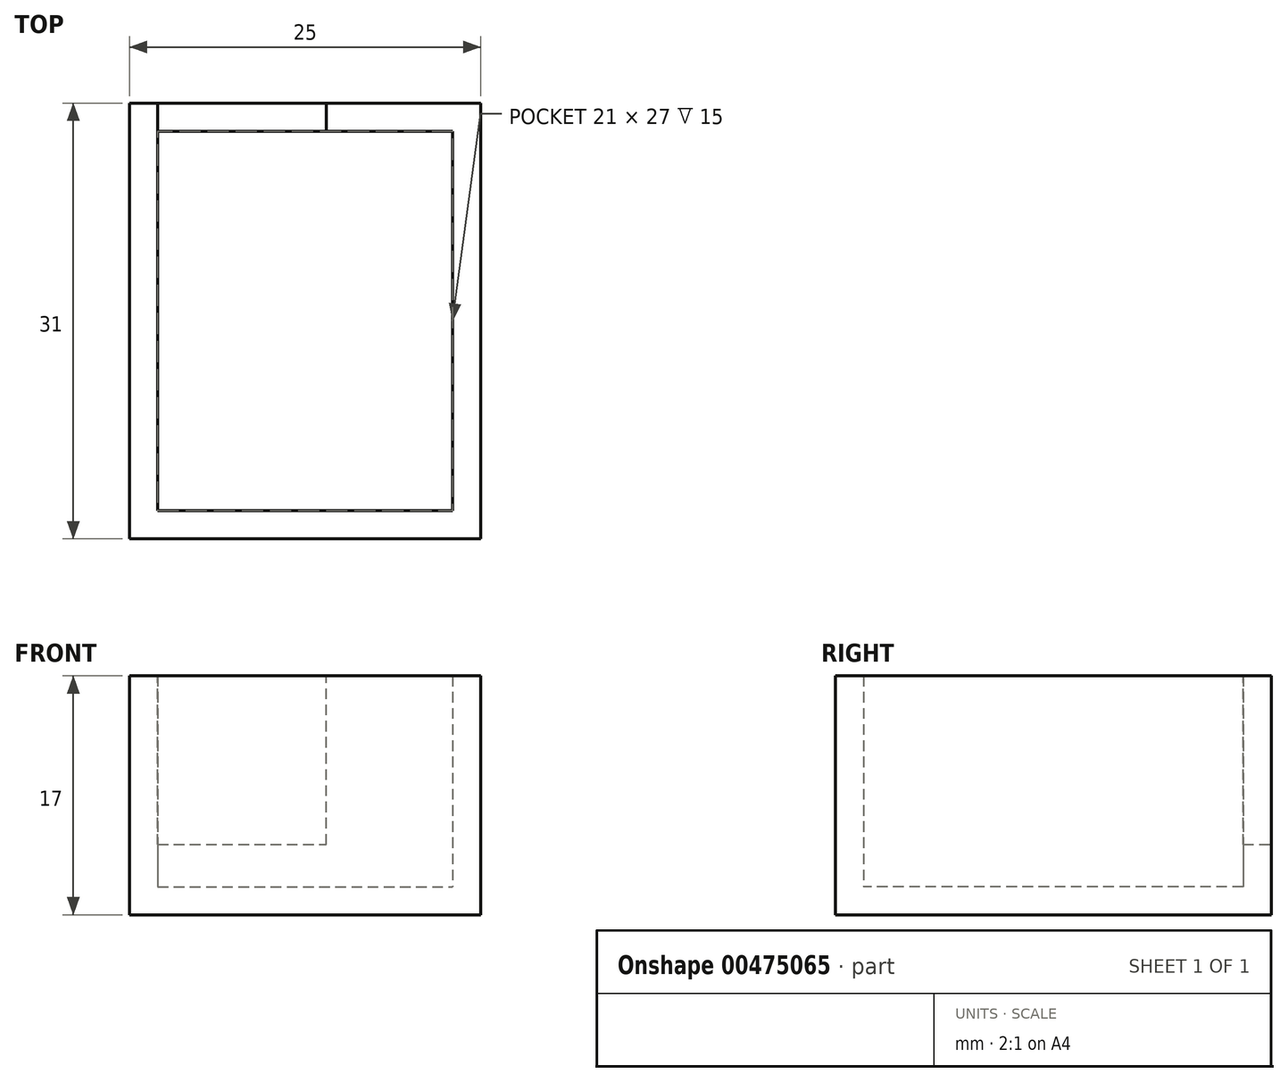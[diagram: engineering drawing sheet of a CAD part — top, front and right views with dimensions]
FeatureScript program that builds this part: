
annotation { "Feature Type Name" : "Feature", "Feature Type Description" : "" }
export const myFeature = defineFeature(function(context is Context, id is Id, definition is map)
    precondition{}
    {
        {
            var Q0;
            Q0=qCreatedBy(makeId("Top.planeOp"),FACE);
            var sketch = newSketch(context, id + "F0", { "sketchPlane" : qUnion([Q0])});
            skLineSegment(sketch, "E0.bottom", {"start": v(-35.56, 21.4) * mm, "end": v(-10.56, 21.4) * mm});
            skLineSegment(sketch, "E0.top", {"start": v(-35.56, -9.6) * mm, "end": v(-10.56, -9.6) * mm});
            skLineSegment(sketch, "E0.left", {"start": v(-35.56, 21.4) * mm, "end": v(-35.56, -9.6) * mm});
            skLineSegment(sketch, "E0.right", {"start": v(-10.56, 21.4) * mm, "end": v(-10.56, -9.6) * mm});
            skSolve(sketch);
        }
        {
            var Q0;
            Q0=makeQuery(id+"F0.imprint","IMPRINT",FACE,{"disambiguationData":[TD([[makeQuery(id+"F0.imprint","IMPRINT",EDGE,{"derivedFrom":sQuery(id+"F0.wireOp",EDGE,"E0.bottom")}),-1.0]])]});
            extrude(context, id + "F1", {"entities" : qUnion([Q0]), "depth" : 17 * mm});
        }
        {
            var Q0;
            Q0=makeQuery(id+"F1.opExtrude","CAP_FACE",FACE,{"disambiguationData":[OSD([sQuery(id+"F0.wireOp",EDGE,"E0.bottom"),sQuery(id+"F0.wireOp",EDGE,"E0.top"),sQuery(id+"F0.wireOp",EDGE,"E0.left"),sQuery(id+"F0.wireOp",EDGE,"E0.right")])],"isStart":false});
            shell(context, id + "F2", {"entities" : qUnion([Q0]), "thickness" : 2 * mm});
        }
        {
            var Q0;
            Q0=makeQuery(id+"F1.opExtrude","CAP_FACE",FACE,{"disambiguationData":[OSD([sQuery(id+"F0.wireOp",EDGE,"E0.bottom"),sQuery(id+"F0.wireOp",EDGE,"E0.top"),sQuery(id+"F0.wireOp",EDGE,"E0.left"),sQuery(id+"F0.wireOp",EDGE,"E0.right")])],"isStart":false});
            var sketch = newSketch(context, id + "F3", { "sketchPlane" : qUnion([Q0])});
            skLineSegment(sketch, "E1.bottom", {"start": v(-33.56, 19.4) * mm, "end": v(-21.56, 19.4) * mm});
            skLineSegment(sketch, "E1.top", {"start": v(-33.56, 21.4) * mm, "end": v(-21.56, 21.4) * mm});
            skLineSegment(sketch, "E1.left", {"start": v(-33.56, 19.4) * mm, "end": v(-33.56, 21.4) * mm});
            skLineSegment(sketch, "E1.right", {"start": v(-21.56, 19.4) * mm, "end": v(-21.56, 21.4) * mm});
            skLineSegment(sketch, "E2.bottom", {"start": v(-35.56, -9.6) * mm, "end": v(-20.56, -9.6) * mm});
            skLineSegment(sketch, "E2.top", {"start": v(-35.56, -7.6) * mm, "end": v(-20.56, -7.6) * mm});
            skLineSegment(sketch, "E2.left", {"start": v(-35.56, -9.6) * mm, "end": v(-35.56, -7.6) * mm});
            skLineSegment(sketch, "E2.right", {"start": v(-20.56, -9.6) * mm, "end": v(-20.56, -7.6) * mm});
            skLineSegment(sketch, "E3.bottom", {"start": v(-20.56, -7.6) * mm, "end": v(-28.56, -7.6) * mm});
            skLineSegment(sketch, "E3.top", {"start": v(-20.56, -9.6) * mm, "end": v(-28.56, -9.6) * mm});
            skLineSegment(sketch, "E3.left", {"start": v(-20.56, -7.6) * mm, "end": v(-20.56, -9.6) * mm});
            skLineSegment(sketch, "E3.right", {"start": v(-28.56, -7.6) * mm, "end": v(-28.56, -9.6) * mm});
            skSolve(sketch);
        }
        {
            var Q0;
            Q0=makeQuery(id+"F3.imprint","IMPRINT",FACE,{"disambiguationData":[TD([[makeQuery(id+"F3.imprint","IMPRINT",EDGE,{"derivedFrom":sQuery(id+"F3.wireOp",EDGE,"E3.bottom")}),-1.0]])]});
            var Q1;
            Q1=makeQuery(id+"F3.imprint","IMPRINT",FACE,{"disambiguationData":[TD([[makeQuery(id+"F3.imprint","IMPRINT",EDGE,{"derivedFrom":sQuery(id+"F3.wireOp",EDGE,"E1.bottom")}),1.0]])]});
            extrude(context, id + "F4", {"entities" : qUnion([Q0, Q1]), "operationType" : NewBodyOperationType.REMOVE, "oppositeDirection" : true, "depth" : 12 * mm});
        }
    });
